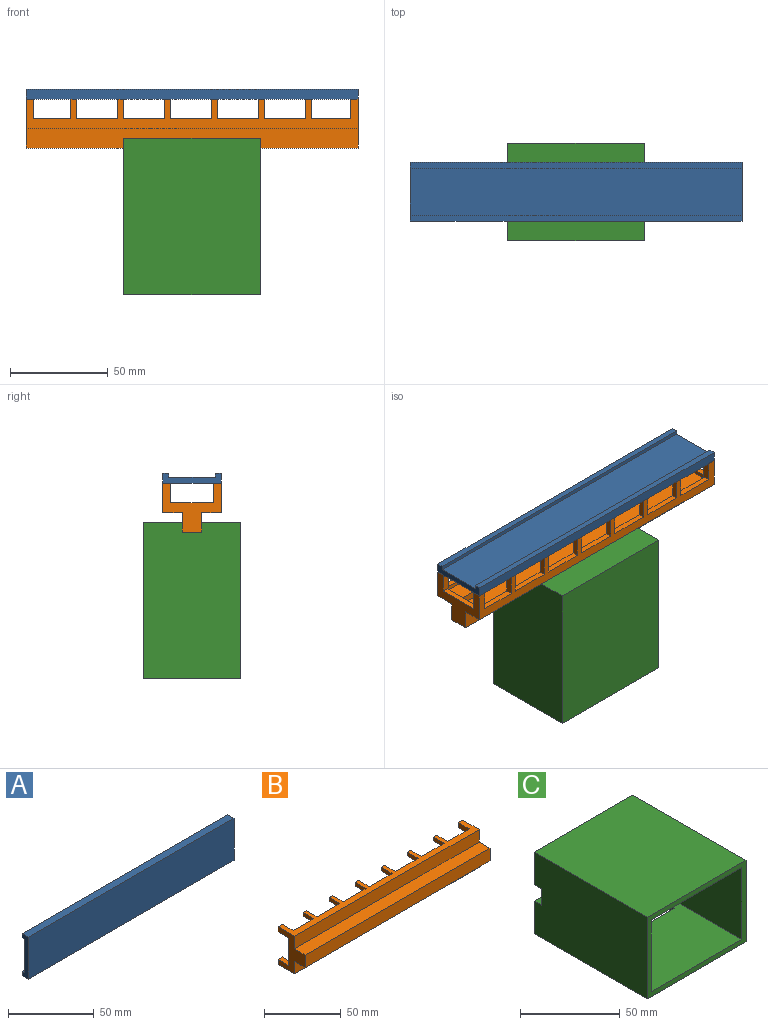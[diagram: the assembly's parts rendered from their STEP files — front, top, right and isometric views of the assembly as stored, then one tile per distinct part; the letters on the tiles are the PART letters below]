
ASSEMBLY  parts=3 mates=2
PART A: 10 faces, bbox 170x5x30 mm
  f0: plane 170x24mm, normal (0,1,0), area 4080mm2, adj f2,f4,f6,f8
  f1: plane 170x5mm, normal (0,0,-1), area 850mm2, adj f2,f4,f5,f7
  f2: plane 30x5mm, normal (-1,0,0), area 102mm2, adj f0,f1,f3,f5,f6,f7,f8,f9
  f3: plane 170x5mm, normal (0,0,1), area 850mm2, adj f2,f4,f5,f9
  f4: plane 30x5mm, normal (1,0,0), area 102mm2, adj f0,f1,f3,f5,f6,f7,f8,f9
  f5: plane 170x30mm, normal (0,-1,0), area 5100mm2, adj f1,f2,f3,f4
  f6: plane 170x2mm, normal (0,0,1), area 340mm2, adj f0,f2,f4,f7
  f7: plane 170x3mm, normal (0,1,0), area 510mm2, adj f1,f2,f4,f6
  f8: plane 170x2mm, normal (0,0,-1), area 340mm2, adj f0,f2,f4,f9
  f9: plane 170x3mm, normal (0,1,0), area 510mm2, adj f2,f3,f4,f8
PART B: 106 faces, bbox 170x25x30 mm
  f0: plane 4x4mm, normal (0,1,0), area 10.2mm2, adj f21,f28,f76,f85,f101,f102,f103,f104
  f1: plane 4x4mm, normal (0,1,0), area 10.2mm2, adj f21,f29,f77,f79,f96,f97,f98,f99
  f2: plane 4x4mm, normal (0,1,0), area 10.2mm2, adj f23,f29,f75,f81,f91,f92,f93,f94
  f3: plane 4x4mm, normal (0,1,0), area 10.2mm2, adj f23,f28,f74,f83,f86,f87,f88,f89
  f4: plane 164x12mm, normal (0,0,-1), area 508mm2, adj f5,f8,f10,f12,f14,f16,f18,f30
  f5: plane 20x3mm, normal (0,1,0), area 60mm2, adj f4,f29,f38,f77
  f6: plane 19x3mm, normal (0,1,0), area 57mm2, adj f28,f37,f72,f74
  f7: plane 21x3mm, normal (0,1,0), area 63mm2, adj f28,f37,f66,f71
  f8: plane 19x3mm, normal (0,1,0), area 57mm2, adj f4,f29,f69,f75
  f9: plane 21x3mm, normal (0,1,0), area 63mm2, adj f28,f37,f60,f65
  f10: plane 21x3mm, normal (0,1,0), area 63mm2, adj f4,f29,f63,f68
  f11: plane 21x3mm, normal (0,1,0), area 63mm2, adj f28,f37,f54,f59
  f12: plane 21x3mm, normal (0,1,0), area 63mm2, adj f4,f29,f57,f62
  f13: plane 21x3mm, normal (0,1,0), area 63mm2, adj f28,f37,f48,f53
  f14: plane 21x3mm, normal (0,1,0), area 63mm2, adj f4,f29,f51,f56
  f15: plane 21x3mm, normal (0,1,0), area 63mm2, adj f28,f37,f42,f47
  f16: plane 21x3mm, normal (0,1,0), area 63mm2, adj f4,f29,f45,f50
  f17: plane 20x3mm, normal (0,1,0), area 60mm2, adj f28,f37,f41,f76
  f18: plane 21x3mm, normal (0,1,0), area 63mm2, adj f4,f29,f39,f44
  f19: plane 22x3mm, normal (0,1,0), area 66mm2, adj f23,f32,f81,f83
  f20: plane 22x3mm, normal (0,1,0), area 66mm2, adj f21,f30,f79,f85
  f21: plane 30x25mm, normal (1,0,0), area 330mm2, adj f0,f1,f20,f22,f24,f25,f26,f27
  f22: plane 170x10mm, normal (0,-1,0), area 1700mm2, adj f21,f23,f24,f25
  f23: plane 30x25mm, normal (-1,0,0), area 330mm2, adj f2,f3,f19,f22,f24,f25,f26,f27
  f24: plane 170x10mm, normal (0,0,-1), area 1700mm2, adj f21,f22,f23,f27
  f25: plane 170x10mm, normal (0,0,1), area 1700mm2, adj f21,f22,f23,f26
  f26: plane 170x10mm, normal (0,-1,0), area 1700mm2, adj f21,f23,f25,f29
  f27: plane 170x10mm, normal (0,-1,0), area 1700mm2, adj f21,f23,f24,f28
  f28: plane 170x15mm, normal (0,0,-1), area 1110mm2, adj f0,f3,f6,f7,f9,f11,f13,f15
  f29: plane 170x15mm, normal (0,0,1), area 1110mm2, adj f1,f2,f5,f8,f10,f12,f14,f16
  f30: plane 24x12mm, normal (-1,0,0), area 88mm2, adj f4,f20,f31,f33,f34,f35,f36,f37
  f31: plane 164x4mm, normal (0,1,0), area 656mm2, adj f30,f32,f33,f34
  f32: plane 24x12mm, normal (1,0,0), area 88mm2, adj f4,f19,f31,f33,f34,f35,f36,f37
  f33: plane 164x10mm, normal (0,0,1), area 1640mm2, adj f30,f31,f32,f36
  f34: plane 164x10mm, normal (0,0,-1), area 1640mm2, adj f30,f31,f32,f35
  f35: plane 164x10mm, normal (0,1,0), area 1640mm2, adj f4,f30,f32,f34
  f36: plane 164x10mm, normal (0,1,0), area 1640mm2, adj f30,f32,f33,f37
  f37: plane 164x12mm, normal (0,0,1), area 508mm2, adj f6,f7,f9,f11,f13,f15,f17,f30
  f38: plane 10x3mm, normal (1,0,0), area 30mm2, adj f4,f5,f29,f40
  f39: plane 10x3mm, normal (-1,0,0), area 30mm2, adj f4,f18,f29,f40
  f40: plane 3x3mm, normal (0,1,0), area 9mm2, adj f4,f29,f38,f39
  f41: plane 10x3mm, normal (1,0,0), area 30mm2, adj f17,f28,f37,f43
  f42: plane 10x3mm, normal (-1,0,0), area 30mm2, adj f15,f28,f37,f43
  f43: plane 3x3mm, normal (0,1,0), area 9mm2, adj f28,f37,f41,f42
  f44: plane 10x3mm, normal (1,0,0), area 30mm2, adj f4,f18,f29,f46
  f45: plane 10x3mm, normal (-1,0,0), area 30mm2, adj f4,f16,f29,f46
  f46: plane 3x3mm, normal (0,1,0), area 9mm2, adj f4,f29,f44,f45
  f47: plane 10x3mm, normal (1,0,0), area 30mm2, adj f15,f28,f37,f49
  f48: plane 10x3mm, normal (-1,0,0), area 30mm2, adj f13,f28,f37,f49
  f49: plane 3x3mm, normal (0,1,0), area 9mm2, adj f28,f37,f47,f48
  f50: plane 10x3mm, normal (1,0,0), area 30mm2, adj f4,f16,f29,f52
  f51: plane 10x3mm, normal (-1,0,0), area 30mm2, adj f4,f14,f29,f52
  f52: plane 3x3mm, normal (0,1,0), area 9mm2, adj f4,f29,f50,f51
  f53: plane 10x3mm, normal (1,0,0), area 30mm2, adj f13,f28,f37,f55
  f54: plane 10x3mm, normal (-1,0,0), area 30mm2, adj f11,f28,f37,f55
  f55: plane 3x3mm, normal (0,1,0), area 9mm2, adj f28,f37,f53,f54
  f56: plane 10x3mm, normal (1,0,0), area 30mm2, adj f4,f14,f29,f58
  f57: plane 10x3mm, normal (-1,0,0), area 30mm2, adj f4,f12,f29,f58
  f58: plane 3x3mm, normal (0,1,0), area 9mm2, adj f4,f29,f56,f57
  f59: plane 10x3mm, normal (1,0,0), area 30mm2, adj f11,f28,f37,f61
  f60: plane 10x3mm, normal (-1,0,0), area 30mm2, adj f9,f28,f37,f61
  f61: plane 3x3mm, normal (0,1,0), area 9mm2, adj f28,f37,f59,f60
  f62: plane 10x3mm, normal (1,0,0), area 30mm2, adj f4,f12,f29,f64
  f63: plane 10x3mm, normal (-1,0,0), area 30mm2, adj f4,f10,f29,f64
  f64: plane 3x3mm, normal (0,1,0), area 9mm2, adj f4,f29,f62,f63
  f65: plane 10x3mm, normal (1,0,0), area 30mm2, adj f9,f28,f37,f67
  f66: plane 10x3mm, normal (-1,0,0), area 30mm2, adj f7,f28,f37,f67
  f67: plane 3x3mm, normal (0,1,0), area 9mm2, adj f28,f37,f65,f66
  f68: plane 10x3mm, normal (1,0,0), area 30mm2, adj f4,f10,f29,f70
  f69: plane 10x3mm, normal (-1,0,0), area 30mm2, adj f4,f8,f29,f70
  f70: plane 3x3mm, normal (0,1,0), area 9mm2, adj f4,f29,f68,f69
  f71: plane 10x3mm, normal (1,0,0), area 30mm2, adj f7,f28,f37,f73
  f72: plane 10x3mm, normal (-1,0,0), area 30mm2, adj f6,f28,f37,f73
  f73: plane 3x3mm, normal (0,1,0), area 9mm2, adj f28,f37,f71,f72
  f74: plane 10x4mm, normal (1,0,0), area 40mm2, adj f3,f6,f28,f82,f83
  f75: plane 10x4mm, normal (1,0,0), area 40mm2, adj f2,f8,f29,f80,f81
  f76: plane 10x4mm, normal (-1,0,0), area 40mm2, adj f0,f17,f28,f84,f85
  f77: plane 10x4mm, normal (-1,0,0), area 40mm2, adj f1,f5,f29,f78,f79
  f78: plane 1x1mm, normal (0,-1,0), area 1mm2, adj f4,f30,f77,f79
  f79: plane 10x4mm, normal (0,0,-1), area 40mm2, adj f1,f20,f21,f77,f78
  f80: plane 1x1mm, normal (0,-1,0), area 1mm2, adj f4,f32,f75,f81
  f81: plane 10x4mm, normal (0,0,-1), area 40mm2, adj f2,f19,f23,f75,f80
  f82: plane 1x1mm, normal (0,-1,0), area 1mm2, adj f32,f37,f74,f83
  f83: plane 10x4mm, normal (0,0,1), area 40mm2, adj f3,f19,f23,f74,f82
  f84: plane 1x1mm, normal (0,-1,0), area 1mm2, adj f30,f37,f76,f85
  f85: plane 10x4mm, normal (0,0,1), area 40mm2, adj f0,f20,f21,f76,f84
  f86: plane 5x2.4mm, normal (0,0,1), area 12mm2, adj f3,f87,f89,f90
  f87: plane 5x2.4mm, normal (1,0,0), area 12mm2, adj f3,f86,f88,f90
  f88: plane 5x2.4mm, normal (0,0,-1), area 12mm2, adj f3,f87,f89,f90
  f89: plane 5x2.4mm, normal (-1,0,0), area 12mm2, adj f3,f86,f88,f90
  f90: plane 2.4x2.4mm, normal (0,1,0), area 5.8mm2, adj f86,f87,f88,f89
  f91: plane 5x2.4mm, normal (1,0,0), area 12mm2, adj f2,f92,f94,f95
  f92: plane 5x2.4mm, normal (0,0,-1), area 12mm2, adj f2,f91,f93,f95
  f93: plane 5x2.4mm, normal (-1,0,0), area 12mm2, adj f2,f92,f94,f95
  f94: plane 5x2.4mm, normal (0,0,1), area 12mm2, adj f2,f91,f93,f95
  f95: plane 2.4x2.4mm, normal (0,1,0), area 5.8mm2, adj f91,f92,f93,f94
  f96: plane 5x2.4mm, normal (1,0,0), area 12mm2, adj f1,f97,f99,f100
  f97: plane 5x2.4mm, normal (0,0,-1), area 12mm2, adj f1,f96,f98,f100
  f98: plane 5x2.4mm, normal (-1,0,0), area 12mm2, adj f1,f97,f99,f100
  f99: plane 5x2.4mm, normal (0,0,1), area 12mm2, adj f1,f96,f98,f100
  f100: plane 2.4x2.4mm, normal (0,1,0), area 5.8mm2, adj f96,f97,f98,f99
  f101: plane 5x2.4mm, normal (-1,0,0), area 12mm2, adj f0,f102,f104,f105
  f102: plane 5x2.4mm, normal (0,0,1), area 12mm2, adj f0,f101,f103,f105
  f103: plane 5x2.4mm, normal (1,0,0), area 12mm2, adj f0,f102,f104,f105
  f104: plane 5x2.4mm, normal (0,0,-1), area 12mm2, adj f0,f101,f103,f105
  f105: plane 2.4x2.4mm, normal (0,1,0), area 5.8mm2, adj f101,f102,f103,f104
PART C: 33 faces, bbox 70x80x50 mm
  f0: plane 77x44mm, normal (-1,0,0), area 3368mm2, adj f2,f6,f26,f27,f28,f30,f31,f32
  f1: plane 77x44mm, normal (1,0,0), area 3368mm2, adj f2,f6,f26,f28,f29,f30,f31,f32
  f2: plane 77x64mm, normal (0,0,-1), area 4928mm2, adj f0,f1,f6,f31
  f3: plane 70x20mm, normal (0,1,0), area 1400mm2, adj f5,f7,f9,f30
  f4: plane 70x20mm, normal (0,1,0), area 1400mm2, adj f5,f7,f8,f28
  f5: plane 80x50mm, normal (-1,0,0), area 3950mm2, adj f3,f4,f6,f8,f9,f28,f29,f30
  f6: plane 70x50mm, normal (0,-1,0), area 684mm2, adj f0,f1,f2,f5,f7,f8,f9,f26
  f7: plane 80x50mm, normal (1,0,0), area 3950mm2, adj f3,f4,f6,f8,f9,f27,f28,f30
  f8: plane 80x70mm, normal (0,0,1), area 5600mm2, adj f4,f5,f6,f7
  f9: plane 80x70mm, normal (0,0,-1), area 4736mm2, adj f3,f5,f6,f7,f10,f11,f12,f13
  f10: plane 12x3mm, normal (-1,0,0), area 36mm2, adj f9,f11,f13,f26
  f11: plane 18x3mm, normal (0,-1,0), area 54mm2, adj f9,f10,f12,f26
  f12: plane 12x3mm, normal (1,0,0), area 36mm2, adj f9,f11,f13,f26
  f13: plane 18x3mm, normal (0,1,0), area 54mm2, adj f9,f10,f12,f26
  f14: plane 18x3mm, normal (0,-1,0), area 54mm2, adj f9,f15,f17,f26
  f15: plane 12x3mm, normal (1,0,0), area 36mm2, adj f9,f14,f16,f26
  f16: plane 18x3mm, normal (0,1,0), area 54mm2, adj f9,f15,f17,f26
  f17: plane 12x3mm, normal (-1,0,0), area 36mm2, adj f9,f14,f16,f26
  f18: plane 18x3mm, normal (0,-1,0), area 54mm2, adj f9,f19,f21,f26
  f19: plane 12x3mm, normal (1,0,0), area 36mm2, adj f9,f18,f20,f26
  f20: plane 18x3mm, normal (0,1,0), area 54mm2, adj f9,f19,f21,f26
  f21: plane 12x3mm, normal (-1,0,0), area 36mm2, adj f9,f18,f20,f26
  f22: plane 12x3mm, normal (-1,0,0), area 36mm2, adj f9,f23,f25,f26
  f23: plane 18x3mm, normal (0,-1,0), area 54mm2, adj f9,f22,f24,f26
  f24: plane 12x3mm, normal (1,0,0), area 36mm2, adj f9,f23,f25,f26
  f25: plane 18x3mm, normal (0,1,0), area 54mm2, adj f9,f22,f24,f26
  f26: plane 77x64mm, normal (0,0,1), area 4064mm2, adj f0,f1,f6,f10,f11,f12,f13,f14
  f27: plane 10x3mm, normal (0,1,0), area 30mm2, adj f0,f7,f28,f30
  f28: plane 70x5mm, normal (0,0,-1), area 222mm2, adj f0,f1,f4,f5,f7,f27,f29,f31
  f29: plane 10x3mm, normal (0,1,0), area 30mm2, adj f1,f5,f28,f30
  f30: plane 70x5mm, normal (0,0,1), area 222mm2, adj f0,f1,f3,f5,f7,f27,f29,f32
  f31: plane 64x17mm, normal (0,-1,0), area 1088mm2, adj f0,f1,f2,f28
  f32: plane 64x17mm, normal (0,-1,0), area 1088mm2, adj f0,f1,f26,f30
PLACE A rot(axis=(1,0,0),90deg) t=(16.74,61.24,-48.31)mm
PLACE B rot(axis=(1,0,0),90deg) t=(16.74,61.24,-48.31)mm
PLACE C rot(axis=(1,0,0),90deg) t=(16.74,61.24,-43.31)mm
MATE fastened A.f5 <-> B.f2  axis (0,0,-1) through (-68.26,21.24,16.69)mm
MATE fastened B.f25 <-> C.f28  axis (0,-1,0) through (16.74,31.24,-8.31)mm
